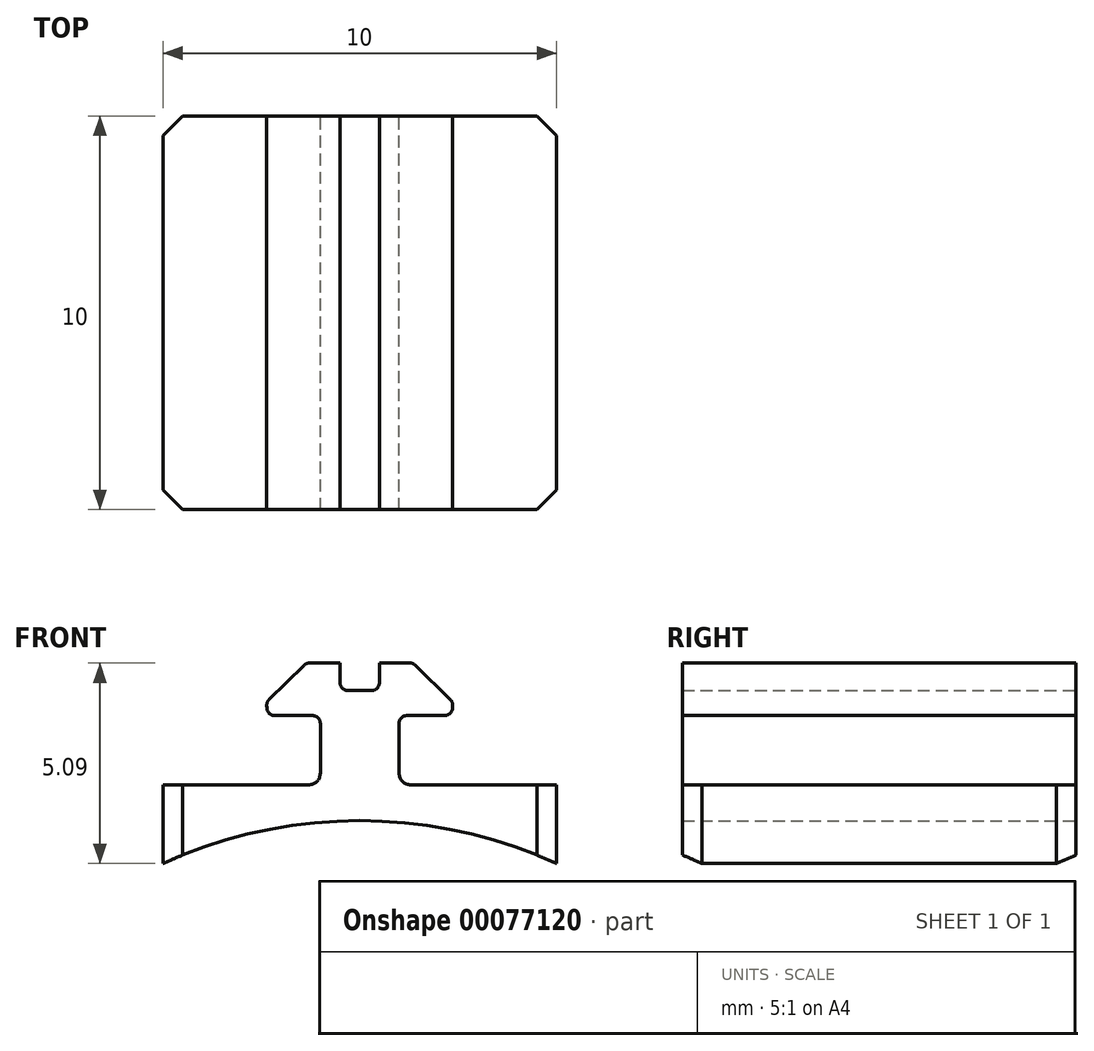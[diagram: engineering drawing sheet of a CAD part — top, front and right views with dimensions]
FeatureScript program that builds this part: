
annotation { "Feature Type Name" : "Feature", "Feature Type Description" : "" }
export const myFeature = defineFeature(function(context is Context, id is Id, definition is map)
    precondition{}
    {
        {
            var Q0;
            Q0=qCreatedBy(makeId("Front.planeOp"),FACE);
            var sketch = newSketch(context, id + "F0", { "sketchPlane" : qUnion([Q0])});
            skLineSegment(sketch, "E0", {"start": v(0, 19.4) * mm, "end": v(0, 3.26) * mm, "construction": true});
            skLineSegment(sketch, "E1", {"start": v(-5, -1.13) * mm, "end": v(-5, 0.87) * mm});
            skLineSegment(sketch, "E2", {"start": v(-5, 0.87) * mm, "end": v(-1, 0.87) * mm});
            skLineSegment(sketch, "E3", {"start": v(-1, 0.87) * mm, "end": v(-1, 2.63) * mm});
            skLineSegment(sketch, "E4", {"start": v(-1, 2.63) * mm, "end": v(-2.35, 2.63) * mm});
            skLineSegment(sketch, "E5", {"start": v(0, 3.36) * mm, "end": v(0, 3.26) * mm});
            skLineSegment(sketch, "E6.MirrorCS", {"start": v(1, 0.87) * mm, "end": v(1, 2.63) * mm});
            skLineSegment(sketch, "E7.MirrorCS", {"start": v(5, 0.87) * mm, "end": v(1, 0.87) * mm});
            skLineSegment(sketch, "E8.MirrorCS", {"start": v(5, -1.13) * mm, "end": v(5, 0.87) * mm});
            skArc(sketch, "E9", {"start": v(5, -1.13) * mm, "mid": v(0, -0.04) * mm, "end": v(-5, -1.13) * mm});
            skPoint(sketch, "E10.MirrorCS.end.orphan", {"position": v(5, -1.13) * mm});
            skPoint(sketch, "E10.MirrorCS.start.orphan", {"position": v(0, 0) * mm});
            skLineSegment(sketch, "E11", {"start": v(-1.36, 3.96) * mm, "end": v(-0.5, 3.96) * mm});
            skLineSegment(sketch, "E12", {"start": v(-2.36, 2.98) * mm, "end": v(-1.36, 3.96) * mm});
            skPoint(sketch, "E13.MirrorCS.end.orphan", {"position": v(0, 3.36) * mm});
            skLineSegment(sketch, "E14.MirrorCS", {"start": v(2.36, 2.98) * mm, "end": v(1.36, 3.96) * mm});
            skPoint(sketch, "E15.MirrorCS.start.orphan", {"position": v(1.36, 3.96) * mm});
            skLineSegment(sketch, "E16", {"start": v(-0.5, 3.96) * mm, "end": v(-0.5, 3.26) * mm});
            skLineSegment(sketch, "E17", {"start": v(-0.5, 3.26) * mm, "end": v(0, 3.26) * mm});
            skLineSegment(sketch, "E18.MirrorCS", {"start": v(0.5, 3.26) * mm, "end": v(0, 3.26) * mm});
            skLineSegment(sketch, "E19.MirrorCS", {"start": v(0.5, 3.96) * mm, "end": v(0.5, 3.26) * mm});
            skLineSegment(sketch, "E20.MirrorCS", {"start": v(1.36, 3.96) * mm, "end": v(0.5, 3.96) * mm});
            skLineSegment(sketch, "E21", {"start": v(-2.36, 2.98) * mm, "end": v(-2.35, 2.63) * mm});
            skPoint(sketch, "E22.MirrorCS.start.orphan", {"position": v(1, 2.63) * mm});
            skPoint(sketch, "E23.MirrorCS.end.orphan", {"position": v(2.36, 2.98) * mm});
            skPoint(sketch, "E23.MirrorCS.start.orphan", {"position": v(3, 2.57) * mm});
            skLineSegment(sketch, "E24.MirrorCS", {"start": v(1, 2.63) * mm, "end": v(2.35, 2.63) * mm});
            skLineSegment(sketch, "E25.MirrorCS", {"start": v(2.36, 2.98) * mm, "end": v(2.35, 2.63) * mm});
            skLineSegment(sketch, "E26.trimOffspring", {"start": v(0, -0.04) * mm, "end": v(0, -16.7) * mm, "construction": true});
            skLineSegment(sketch, "E27.trimOffspring", {"start": v(0, 0) * mm, "end": v(0, -0.04) * mm});
            skSolve(sketch);
        }
        {
            var Q0;
            {var subQ1=sQuery(id+"F0.wireOp",EDGE,"E1");Q0=makeQuery(id+"F0.imprint","IMPRINT",FACE,{"disambiguationData":[TD([[makeQuery(id+"F0.imprint","IMPRINT",EDGE,{"derivedFrom":subQ1}),-1.0]])]});}
            var Q1;
            Q1=makeQuery(id+"F0.imprint","IMPRINT",FACE,{"disambiguationData":[TD([[makeQuery(id+"F0.imprint","IMPRINT",EDGE,{"derivedFrom":sQuery(id+"F0.wireOp",EDGE,"E22.MirrorCS")}),1.0]])]});
            extrude(context, id + "F1", {"entities" : qUnion([Q0, Q1]), "depth" : 10 * mm});
        }
        {
            var Q0;
            Q0=makeQuery(id+"F1.opExtrude","SWEPT_EDGE",EDGE,{"disambiguationData":[OSD([sQuery(id+"F0.wireOp",EDGE,"E16"),sQuery(id+"F0.wireOp",EDGE,"E17")])]});
            var Q1;
            Q1=makeQuery(id+"F1.opExtrude","SWEPT_EDGE",EDGE,{"disambiguationData":[OSD([sQuery(id+"F0.wireOp",EDGE,"E18.MirrorCS"),sQuery(id+"F0.wireOp",EDGE,"E19.MirrorCS")])]});
            var Q2;
            Q2=makeQuery(id+"F1.opExtrude","SWEPT_EDGE",EDGE,{"disambiguationData":[OSD([sQuery(id+"F0.wireOp",EDGE,"E14.MirrorCS"),sQuery(id+"F0.wireOp",EDGE,"E23.MirrorCS")])]});
            var Q3;
            Q3=makeQuery(id+"F1.opExtrude","SWEPT_EDGE",EDGE,{"disambiguationData":[OSD([sQuery(id+"F0.wireOp",EDGE,"E22.MirrorCS"),sQuery(id+"F0.wireOp",EDGE,"E23.MirrorCS")])]});
            var Q4;
            Q4=makeQuery(id+"F1.opExtrude","SWEPT_EDGE",EDGE,{"disambiguationData":[OSD([sQuery(id+"F0.wireOp",EDGE,"Fh4L0hf9-FOak-96oc-pc29-sX1zGtYwSFka"),sQuery(id+"F0.wireOp",EDGE,"E12")])]});
            var Q5;
            Q5=makeQuery(id+"F1.opExtrude","SWEPT_EDGE",EDGE,{"disambiguationData":[OSD([sQuery(id+"F0.wireOp",EDGE,"E4"),sQuery(id+"F0.wireOp",EDGE,"Fh4L0hf9-FOak-96oc-pc29-sX1zGtYwSFka")])]});
            var Q6;
            Q6=makeQuery(id+"F1.opExtrude","SWEPT_EDGE",EDGE,{"disambiguationData":[OSD([sQuery(id+"F0.wireOp",EDGE,"E24.MirrorCS"),sQuery(id+"F0.wireOp",EDGE,"E25.MirrorCS")])]});
            var Q7;
            Q7=makeQuery(id+"F1.opExtrude","SWEPT_EDGE",EDGE,{"disambiguationData":[OSD([sQuery(id+"F0.wireOp",EDGE,"E6.MirrorCS"),sQuery(id+"F0.wireOp",EDGE,"E24.MirrorCS")])]});
            fillet(context, id + "F2", {"entities" : qUnion([Q0, Q1, Q2, Q3, Q4, Q5, Q6, Q7]), "radius" : .2 * mm, "tangentPropagation" : true, "allowEdgeOverflow" : false});
        }
        {
            var Q0;
            Q0=makeQuery(id+"F1.opExtrude","SWEPT_EDGE",EDGE,{"disambiguationData":[OSD([sQuery(id+"F0.wireOp",EDGE,"E3"),sQuery(id+"F0.wireOp",EDGE,"E4")])]});
            var Q1;
            Q1=makeQuery(id+"F1.opExtrude","SWEPT_EDGE",EDGE,{"disambiguationData":[OSD([sQuery(id+"F0.wireOp",EDGE,"E2"),sQuery(id+"F0.wireOp",EDGE,"E3")])]});
            var Q2;
            Q2=makeQuery(id+"F1.opExtrude","SWEPT_EDGE",EDGE,{"disambiguationData":[OSD([sQuery(id+"F0.wireOp",EDGE,"E22.MirrorCS"),sQuery(id+"F0.wireOp",EDGE,"E6.MirrorCS")])]});
            var Q3;
            Q3=makeQuery(id+"F1.opExtrude","SWEPT_EDGE",EDGE,{"disambiguationData":[OSD([sQuery(id+"F0.wireOp",EDGE,"E6.MirrorCS"),sQuery(id+"F0.wireOp",EDGE,"E7.MirrorCS")])]});
            fillet(context, id + "F3", {"entities" : qUnion([Q0, Q1, Q2, Q3]), "radius" : .3 * mm, "tangentPropagation" : true, "allowEdgeOverflow" : false});
        }
        {
            var Q0;
            Q0=makeQuery(id+"F1.opExtrude","CAP_EDGE",EDGE,{"disambiguationData":[OSD([sQuery(id+"F0.wireOp",EDGE,"E1")])],"isStart":false});
            var Q1;
            Q1=makeQuery(id+"F1.opExtrude","CAP_EDGE",EDGE,{"disambiguationData":[OSD([sQuery(id+"F0.wireOp",EDGE,"E8.MirrorCS")])],"isStart":false});
            var Q2;
            Q2=makeQuery(id+"F1.opExtrude","CAP_EDGE",EDGE,{"disambiguationData":[OSD([sQuery(id+"F0.wireOp",EDGE,"E8.MirrorCS")])],"isStart":true});
            var Q3;
            Q3=makeQuery(id+"F1.opExtrude","CAP_EDGE",EDGE,{"disambiguationData":[OSD([sQuery(id+"F0.wireOp",EDGE,"E1")])],"isStart":true});
            chamfer(context, id + "F4", {"entities" : qUnion([Q0, Q1, Q2, Q3]), "width" : .5 * mm, "tangentPropagation" : true});
        }
    });
